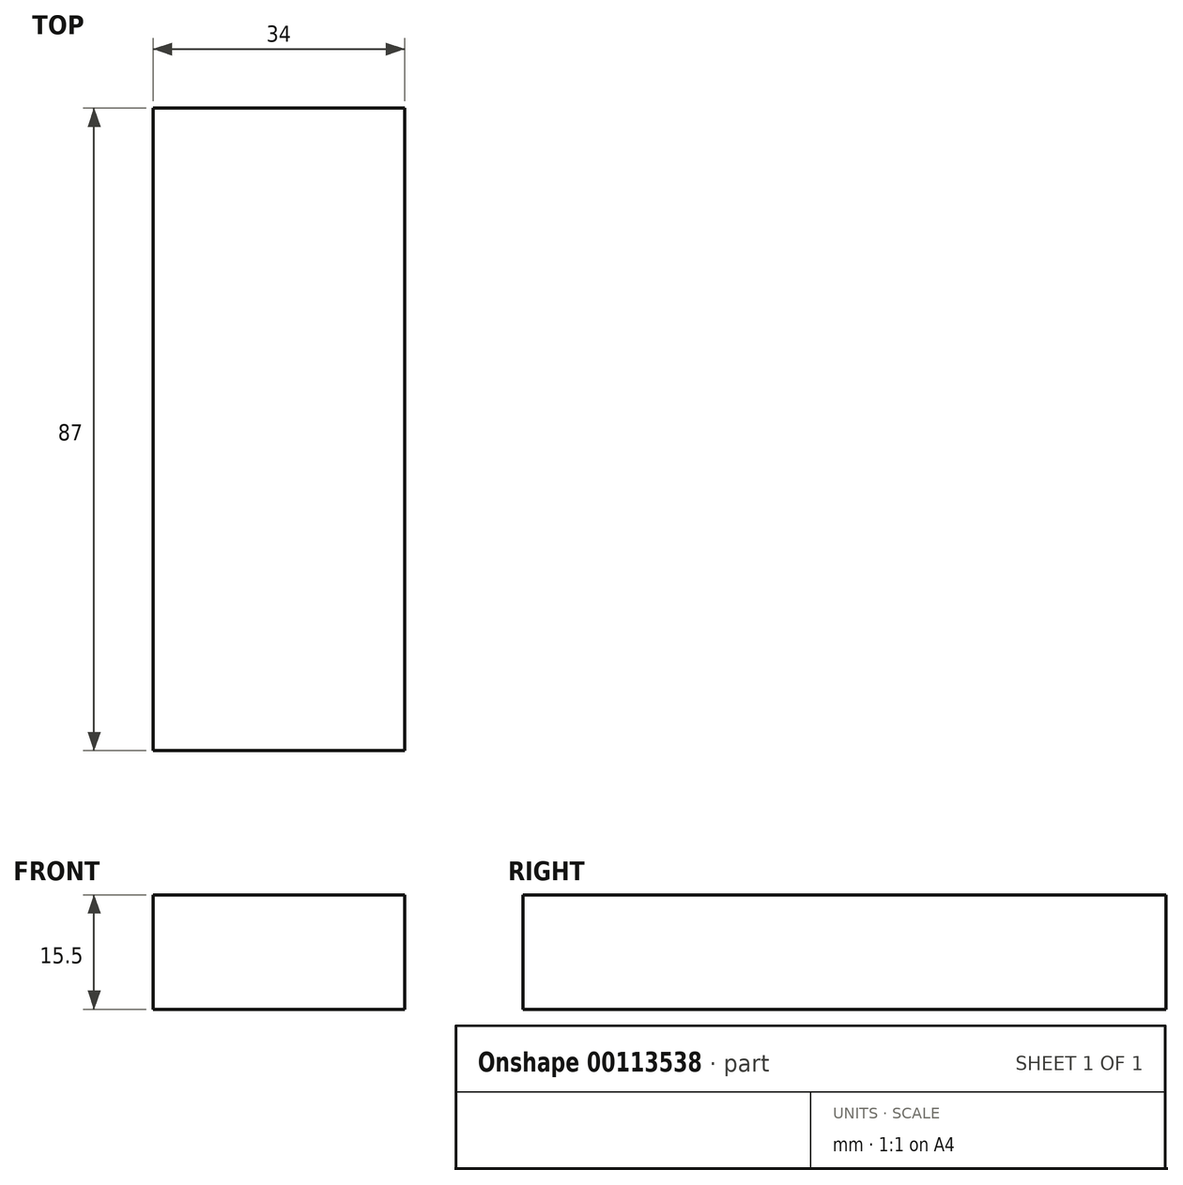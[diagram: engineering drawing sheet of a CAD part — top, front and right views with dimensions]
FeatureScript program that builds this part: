
annotation { "Feature Type Name" : "Feature", "Feature Type Description" : "" }
export const myFeature = defineFeature(function(context is Context, id is Id, definition is map)
    precondition{}
    {
        {
            var Q0;
            Q0=qCreatedBy(makeId("Top.planeOp"),FACE);
            var sketch = newSketch(context, id + "F0", { "sketchPlane" : qUnion([Q0])});
            skLineSegment(sketch, "E0.bottom", {"start": v(17, 43.5) * mm, "end": v(-17, 43.5) * mm});
            skLineSegment(sketch, "E0.top", {"start": v(17, -43.5) * mm, "end": v(-17, -43.5) * mm});
            skLineSegment(sketch, "E0.left", {"start": v(17, 43.5) * mm, "end": v(17, -43.5) * mm});
            skLineSegment(sketch, "E0.right", {"start": v(-17, 43.5) * mm, "end": v(-17, -43.5) * mm});
            skPoint(sketch, "E0.middle", {"position": v(0, 0) * mm});
            skSolve(sketch);
        }
        {
            var Q0;
            Q0=qSketchRegion(id+"F0",true);
            extrude(context, id + "F1", {"entities" : qUnion([Q0]), "depth" : 15.5 * mm});
        }
    });
